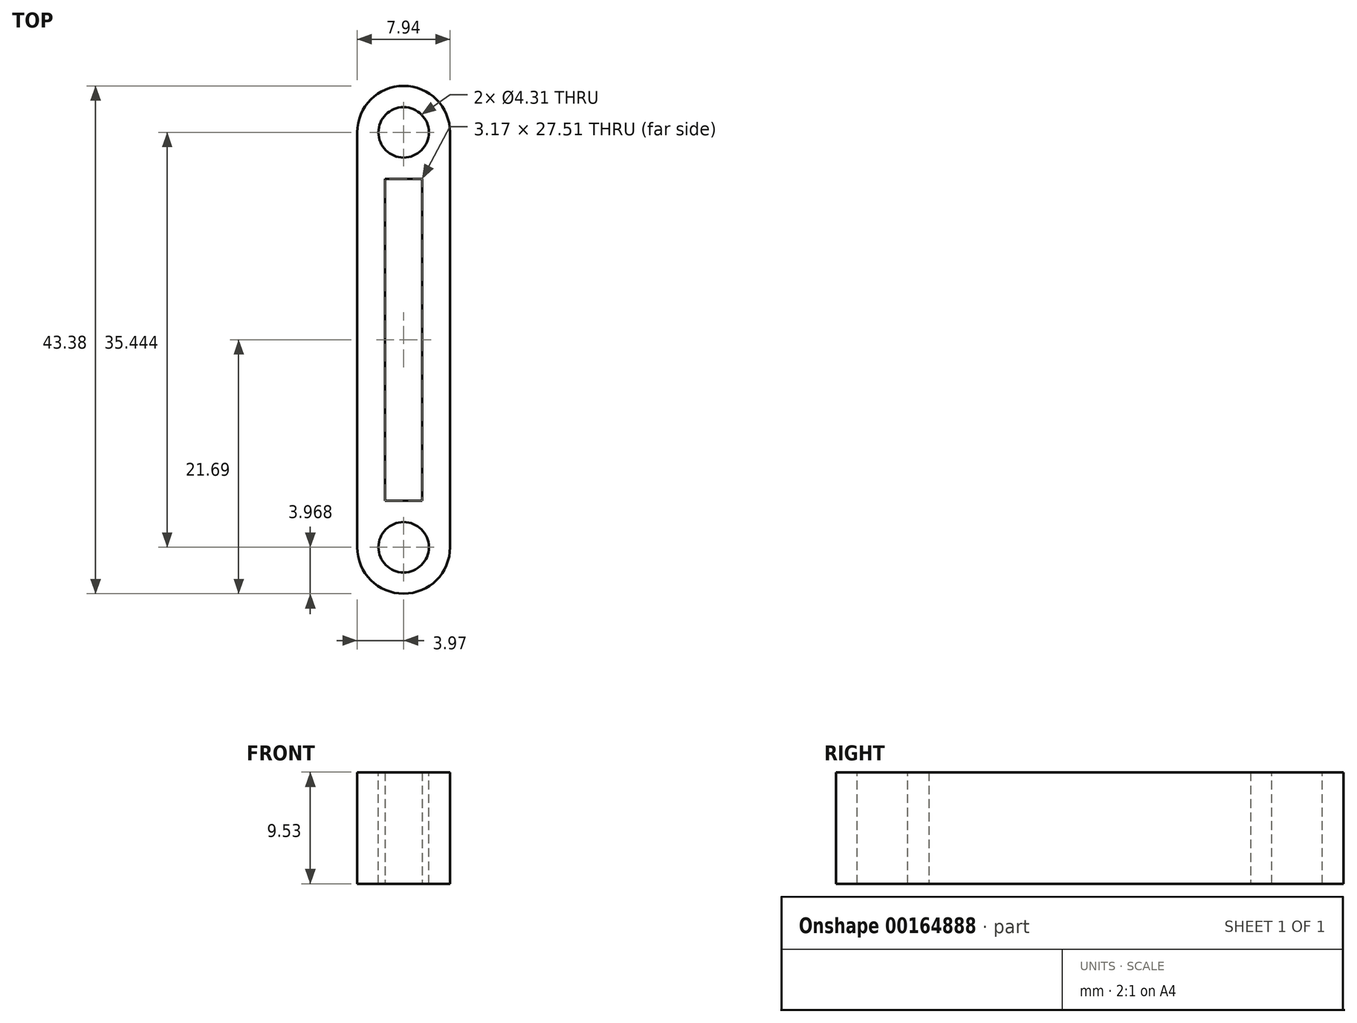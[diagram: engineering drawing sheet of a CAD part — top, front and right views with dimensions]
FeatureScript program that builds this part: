
annotation { "Feature Type Name" : "Feature", "Feature Type Description" : "" }
export const myFeature = defineFeature(function(context is Context, id is Id, definition is map)
    precondition{}
    {
        {
            var Q0;
            Q0=qCreatedBy(makeId("Top.planeOp"),FACE);
            var sketch = newSketch(context, id + "F0", { "sketchPlane" : qUnion([Q0])});
            skLineSegment(sketch, "E0.bottom", {"start": v(3.97, 21.7) * mm, "end": v(-3.97, 21.7) * mm});
            skLineSegment(sketch, "E0.top", {"start": v(3.97, -21.7) * mm, "end": v(-3.97, -21.7) * mm});
            skLineSegment(sketch, "E0.left", {"start": v(3.97, 21.7) * mm, "end": v(3.97, -21.7) * mm});
            skLineSegment(sketch, "E0.right", {"start": v(-3.97, 21.7) * mm, "end": v(-3.97, -21.7) * mm});
            skPoint(sketch, "E0.middle", {"position": v(0, 0) * mm});
            skLineSegment(sketch, "E1.bottom", {"start": v(1.59, 13.75) * mm, "end": v(-1.59, 13.75) * mm});
            skLineSegment(sketch, "E1.top", {"start": v(1.59, -13.75) * mm, "end": v(-1.59, -13.75) * mm});
            skLineSegment(sketch, "E1.left", {"start": v(1.59, 13.75) * mm, "end": v(1.59, -13.75) * mm});
            skLineSegment(sketch, "E1.right", {"start": v(-1.59, 13.75) * mm, "end": v(-1.59, -13.75) * mm});
            skSolve(sketch);
        }
        {
            var Q0;
            Q0=qSketchRegion(id+"F0",true);
            extrude(context, id + "F1", {"entities" : qUnion([Q0]), "depth" : 9.52 * mm});
        }
        {
            var Q0;
            Q0=makeQuery(id+"F1.opExtrude","CAP_FACE",FACE,{"disambiguationData":[OSD([sQuery(id+"F0.wireOp",EDGE,"E0.bottom"),sQuery(id+"F0.wireOp",EDGE,"E0.top"),sQuery(id+"F0.wireOp",EDGE,"E0.left"),sQuery(id+"F0.wireOp",EDGE,"E0.right"),sQuery(id+"F0.wireOp",EDGE,"E1.bottom"),sQuery(id+"F0.wireOp",EDGE,"E1.top"),sQuery(id+"F0.wireOp",EDGE,"E1.left"),sQuery(id+"F0.wireOp",EDGE,"E1.right")])],"isStart":false});
            var sketch = newSketch(context, id + "F2", { "sketchPlane" : qUnion([Q0])});
            skLineSegment(sketch, "E2.bottom", {"start": v(0, 21.7) * mm, "end": v(3.97, 21.7) * mm, "construction": true});
            skLineSegment(sketch, "E2.top", {"start": v(0, 17.72) * mm, "end": v(3.97, 17.72) * mm, "construction": true});
            skLineSegment(sketch, "E2.left", {"start": v(0, 21.7) * mm, "end": v(0, 17.72) * mm, "construction": true});
            skLineSegment(sketch, "E2.right", {"start": v(3.97, 21.7) * mm, "end": v(3.97, 17.72) * mm, "construction": true});
            skLineSegment(sketch, "E3.bottom", {"start": v(0, -21.7) * mm, "end": v(3.97, -21.7) * mm, "construction": true});
            skLineSegment(sketch, "E3.top", {"start": v(0, -17.72) * mm, "end": v(3.97, -17.72) * mm, "construction": true});
            skLineSegment(sketch, "E3.left", {"start": v(0, -21.7) * mm, "end": v(0, -17.72) * mm, "construction": true});
            skLineSegment(sketch, "E3.right", {"start": v(3.97, -21.7) * mm, "end": v(3.97, -17.72) * mm, "construction": true});
            skCircle(sketch, "E4", {"center": v(0, 17.72) * mm, "radius": 2.15 * mm});
            skCircle(sketch, "E5", {"center": v(0, -17.72) * mm, "radius": 2.15 * mm});
            skSolve(sketch);
        }
        {
            var Q0;
            Q0=qSketchRegion(id+"F2",true);
            var Q1;
            Q1=makeQuery(id+"F1.opExtrude","CAP_FACE",FACE,{"disambiguationData":[OSD([sQuery(id+"F0.wireOp",EDGE,"E0.bottom"),sQuery(id+"F0.wireOp",EDGE,"E0.top"),sQuery(id+"F0.wireOp",EDGE,"E0.left"),sQuery(id+"F0.wireOp",EDGE,"E0.right"),sQuery(id+"F0.wireOp",EDGE,"E1.bottom"),sQuery(id+"F0.wireOp",EDGE,"E1.top"),sQuery(id+"F0.wireOp",EDGE,"E1.left"),sQuery(id+"F0.wireOp",EDGE,"E1.right")])],"isStart":true});
            extrude(context, id + "F3", {"entities" : qUnion([Q0]), "operationType" : NewBodyOperationType.REMOVE, "endBound" : BoundingType.UP_TO_SURFACE, "oppositeDirection" : true, "endBoundEntityFace" : qUnion([Q1]), "depth" : 25.4 * mm});
        }
        {
            var Q0;
            Q0=makeQuery(id+"F1.opExtrude","SWEPT_EDGE",EDGE,{"disambiguationData":[OSD([sQuery(id+"F0.wireOp",EDGE,"E0.top"),sQuery(id+"F0.wireOp",EDGE,"E0.right")])]});
            var Q1;
            Q1=makeQuery(id+"F1.opExtrude","SWEPT_EDGE",EDGE,{"disambiguationData":[OSD([sQuery(id+"F0.wireOp",EDGE,"E0.top"),sQuery(id+"F0.wireOp",EDGE,"E0.left")])]});
            var Q2;
            Q2=makeQuery(id+"F1.opExtrude","SWEPT_EDGE",EDGE,{"disambiguationData":[OSD([sQuery(id+"F0.wireOp",EDGE,"E0.bottom"),sQuery(id+"F0.wireOp",EDGE,"E0.left")])]});
            var Q3;
            Q3=makeQuery(id+"F1.opExtrude","SWEPT_EDGE",EDGE,{"disambiguationData":[OSD([sQuery(id+"F0.wireOp",EDGE,"E0.bottom"),sQuery(id+"F0.wireOp",EDGE,"E0.right")])]});
            fillet(context, id + "F4", {"entities" : qUnion([Q0, Q1, Q2, Q3]), "radius" : 3.97 * mm, "tangentPropagation" : true, "allowEdgeOverflow" : false});
        }
    });
